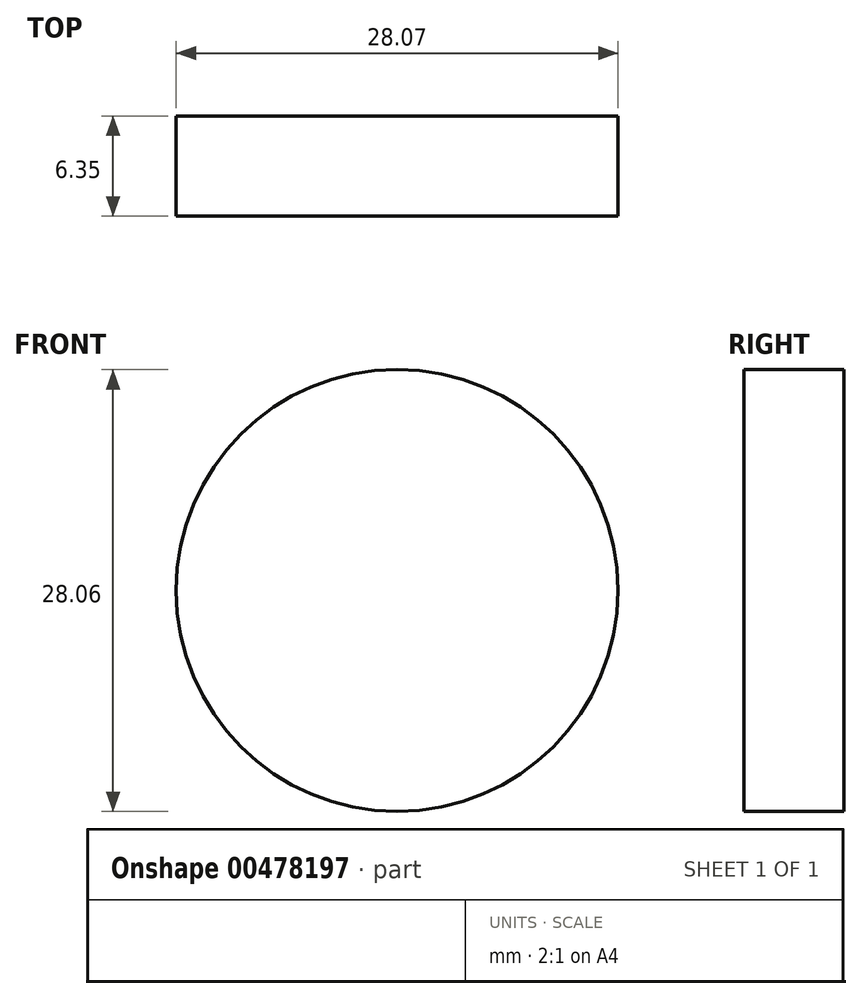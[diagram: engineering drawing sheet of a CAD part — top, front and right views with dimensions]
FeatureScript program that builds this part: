
annotation { "Feature Type Name" : "Feature", "Feature Type Description" : "" }
export const myFeature = defineFeature(function(context is Context, id is Id, definition is map)
    precondition{}
    {
        {
            var Q0;
            Q0=qCreatedBy(makeId("Front.planeOp"),FACE);
            var sketch = newSketch(context, id + "F0", { "sketchPlane" : qUnion([Q0])});
            skCircle(sketch, "E0", {"center": v(-29.5, -22.15) * mm, "radius": 14.03 * mm});
            skSolve(sketch);
        }
        {
            var Q0;
            Q0=makeQuery(id+"F0.imprint","IMPRINT",FACE,{"disambiguationData":[TD([[makeQuery(id+"F0.imprint","IMPRINT",EDGE,{"derivedFrom":sQuery(id+"F0.wireOp",EDGE,"E0")}),1.0]])]});
            extrude(context, id + "F1", {"entities" : qUnion([Q0]), "depth" : 6.35 * mm});
        }
        {
            var Q0;
            Q0=makeQuery(id+"F1.opExtrude","SWEPT_BODY",BODY,{"disambiguationData":[OSD([sQuery(id+"F0.wireOp",EDGE,"E0")])]});
            transform(context, id + "F2", {"entities" : qUnion([Q0]), "transformType" : TransformType.TRANSLATION_3D, "dx" : 0 * mm, "dy" : 0 * mm, "dz" : 0 * mm, "makeCopy" : true});
        }
    });
